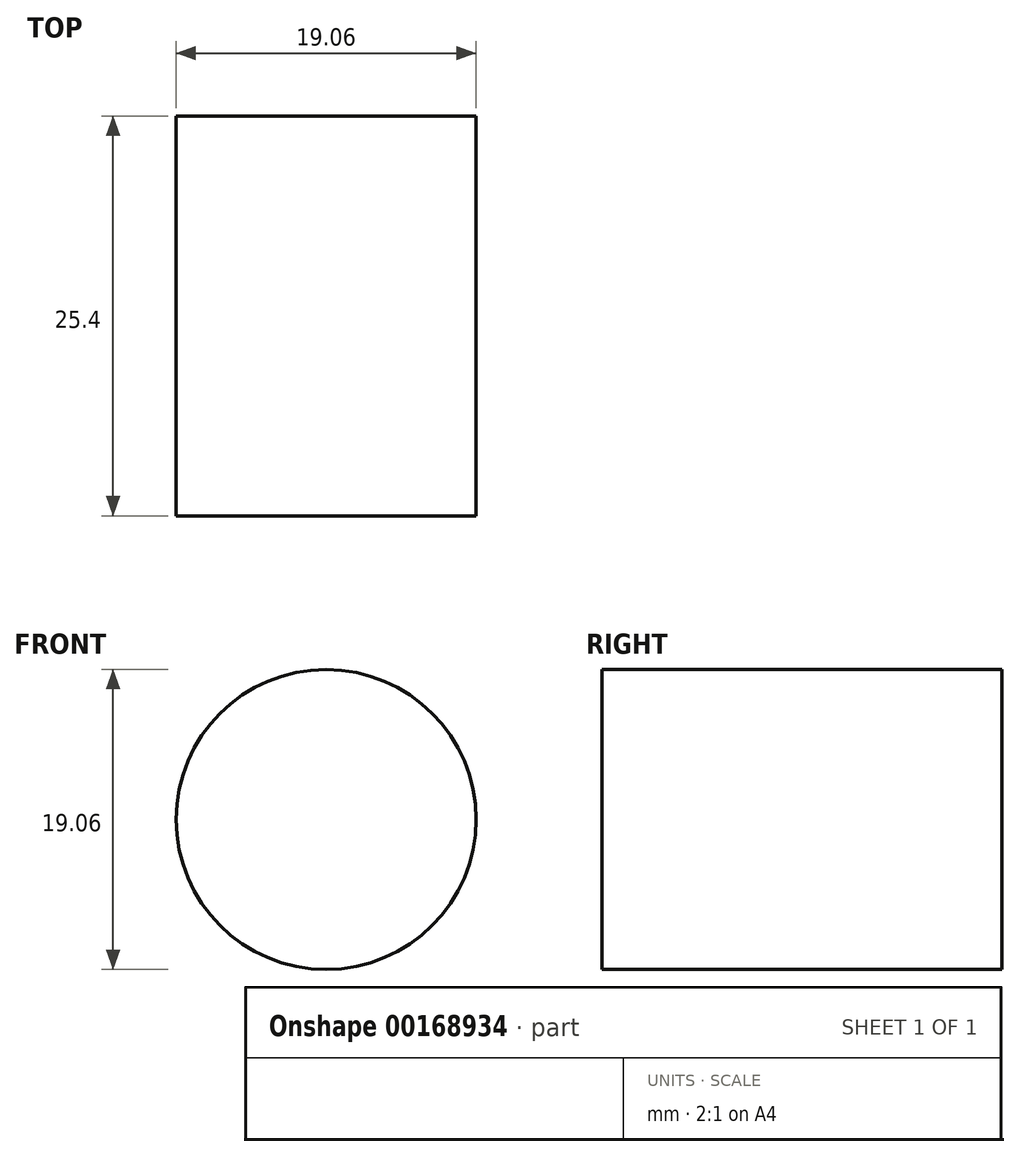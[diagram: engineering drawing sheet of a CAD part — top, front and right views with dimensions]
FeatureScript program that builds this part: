
annotation { "Feature Type Name" : "Feature", "Feature Type Description" : "" }
export const myFeature = defineFeature(function(context is Context, id is Id, definition is map)
    precondition{}
    {
        {
            var Q0;
            Q0=qCreatedBy(makeId("Front.planeOp"),FACE);
            var sketch = newSketch(context, id + "F0", { "sketchPlane" : qUnion([Q0])});
            skCircle(sketch, "E0", {"center": v(0, 0) * mm, "radius": 9.53 * mm});
            skSolve(sketch);
        }
        {
            var Q0;
            Q0=sQuery(id+"F0.wireOp",EDGE,"E0");
            extrude(context, id + "F1", {"bodyType" : ToolBodyType.SURFACE, "surfaceEntities" : qUnion([Q0]), "depth" : 25.4 * mm});
        }
    });
